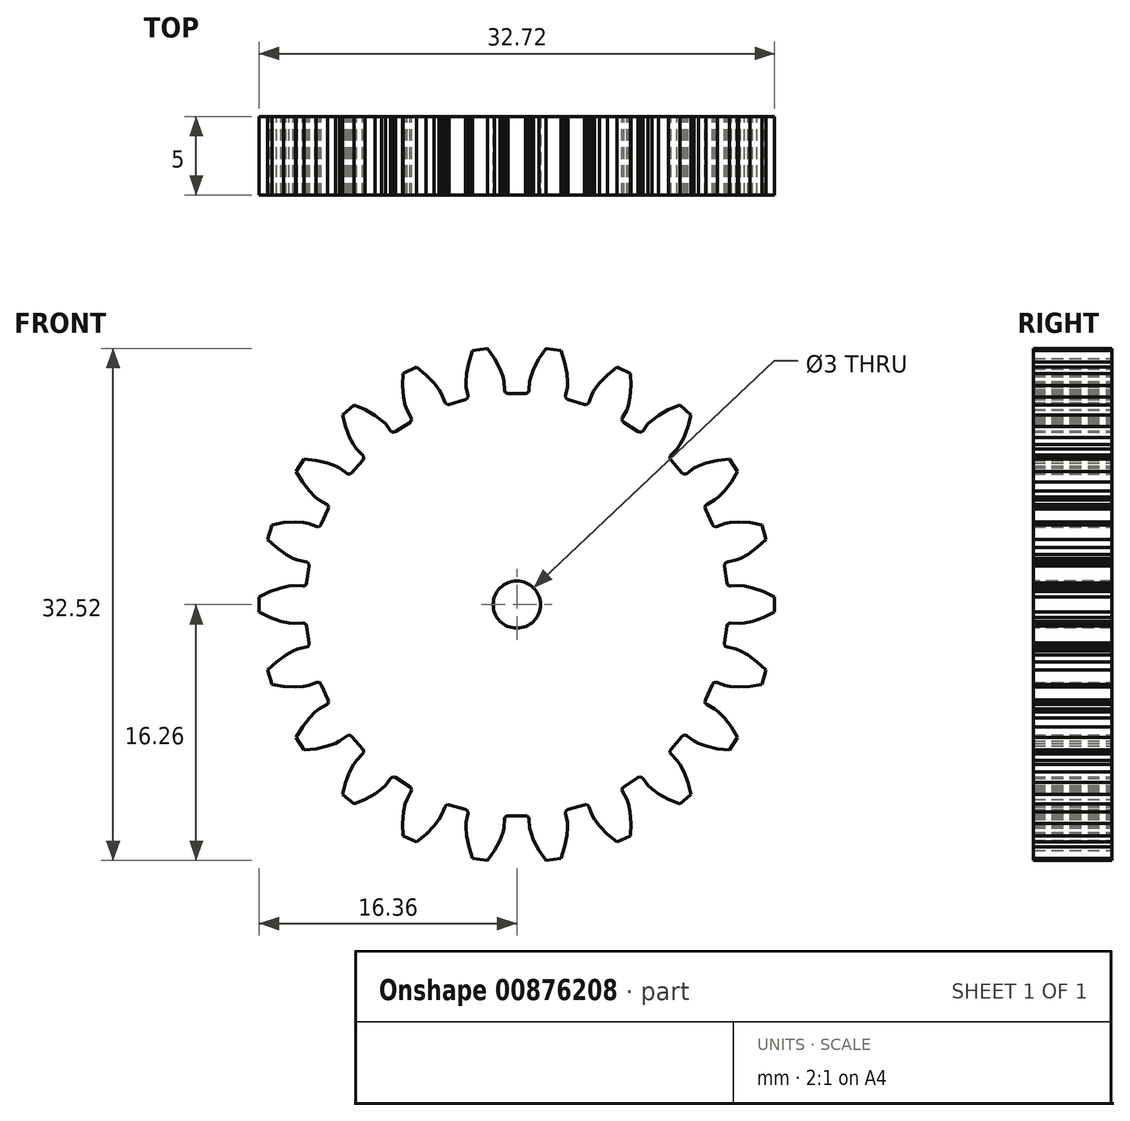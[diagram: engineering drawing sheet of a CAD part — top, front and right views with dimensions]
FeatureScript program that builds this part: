
annotation { "Feature Type Name" : "Feature", "Feature Type Description" : "" }
export const myFeature = defineFeature(function(context is Context, id is Id, definition is map)
    precondition{}
    {
        {
            var Q0;
            Q0=qCreatedBy(makeId("Front.planeOp"),FACE);
            var sketch = newSketch(context, id + "F0", { "sketchPlane" : qUnion([Q0])});
            skLineSegment(sketch, "E0", {"start": v(3.19, -14.67) * mm, "end": v(3.23, -14.15) * mm});
            skLineSegment(sketch, "E1", {"start": v(1.85, 16.26) * mm, "end": v(1.42, 15.62) * mm});
            skLineSegment(sketch, "E2", {"start": v(3.1, 13.28) * mm, "end": v(3.22, 13.83) * mm});
            skLineSegment(sketch, "E3", {"start": v(5.25, 14.06) * mm, "end": v(4.93, 13.65) * mm});
            skLineSegment(sketch, "E4", {"start": v(-9, -12.02) * mm, "end": v(-8.58, -11.7) * mm});
            skLineSegment(sketch, "E5", {"start": v(6.8, -11.58) * mm, "end": v(7.7, -10.99) * mm});
            skLineSegment(sketch, "E6", {"start": v(14.2, -2.94) * mm, "end": v(13.92, -2.82) * mm});
            skLineSegment(sketch, "E7", {"start": v(-0.54, 13.41) * mm, "end": v(-0.65, 13.44) * mm});
            skLineSegment(sketch, "E8", {"start": v(0.54, 13.41) * mm, "end": v(-0.54, 13.41) * mm});
            skLineSegment(sketch, "E9", {"start": v(-0.81, 14.18) * mm, "end": v(-0.89, 14.48) * mm});
            skLineSegment(sketch, "E10", {"start": v(-0.65, 13.44) * mm, "end": v(-0.74, 13.5) * mm});
            skLineSegment(sketch, "E11", {"start": v(-6.71, 11.66) * mm, "end": v(-6.8, 11.58) * mm});
            skLineSegment(sketch, "E12", {"start": v(0.81, 14.18) * mm, "end": v(0.77, 13.61) * mm});
            skLineSegment(sketch, "E13", {"start": v(-9.73, -9.3) * mm, "end": v(-9.73, -9.4) * mm});
            skLineSegment(sketch, "E14", {"start": v(3.1, 13.17) * mm, "end": v(3.1, 13.28) * mm});
            skLineSegment(sketch, "E15", {"start": v(4.57, 12.85) * mm, "end": v(4.51, 12.75) * mm});
            skLineSegment(sketch, "E16", {"start": v(0.89, 14.48) * mm, "end": v(0.81, 14.18) * mm});
            skLineSegment(sketch, "E17", {"start": v(-7.23, -14.68) * mm, "end": v(-6.36, -15.08) * mm});
            skLineSegment(sketch, "E18", {"start": v(-8.58, -11.7) * mm, "end": v(-8.35, -11.49) * mm});
            skLineSegment(sketch, "E19", {"start": v(-1.42, 15.62) * mm, "end": v(-1.85, 16.26) * mm});
            skLineSegment(sketch, "E20", {"start": v(-5.25, -14.06) * mm, "end": v(-4.93, -13.65) * mm});
            skLineSegment(sketch, "E21", {"start": v(3.04, 15.4) * mm, "end": v(2.8, 16.12) * mm});
            skLineSegment(sketch, "E22", {"start": v(-0.74, 13.5) * mm, "end": v(-0.77, 13.61) * mm});
            skLineSegment(sketch, "E23", {"start": v(14.07, -5.24) * mm, "end": v(14.8, -5.2) * mm});
            skLineSegment(sketch, "E24", {"start": v(-4.51, -12.75) * mm, "end": v(-4.41, -12.7) * mm});
            skLineSegment(sketch, "E25", {"start": v(-12.06, -6.36) * mm, "end": v(-12.56, -6.63) * mm});
            skLineSegment(sketch, "E26", {"start": v(-13.4, 1.27) * mm, "end": v(-13.48, 1.2) * mm});
            skLineSegment(sketch, "E27", {"start": v(-0.77, 13.61) * mm, "end": v(-0.81, 14.18) * mm});
            skLineSegment(sketch, "E28", {"start": v(-1.08, 14.97) * mm, "end": v(-1.42, 15.62) * mm});
            skLineSegment(sketch, "E29", {"start": v(-8, -11.04) * mm, "end": v(-7.92, -10.97) * mm});
            skLineSegment(sketch, "E30", {"start": v(-6.8, -11.58) * mm, "end": v(-6.71, -11.66) * mm});
            skLineSegment(sketch, "E31", {"start": v(-14.67, 3.2) * mm, "end": v(-14.2, 2.94) * mm});
            skLineSegment(sketch, "E32", {"start": v(-3.19, -14.67) * mm, "end": v(-3.04, -15.4) * mm});
            skLineSegment(sketch, "E33", {"start": v(0.54, -13.41) * mm, "end": v(0.65, -13.44) * mm});
            skLineSegment(sketch, "E34", {"start": v(-15.26, 3.63) * mm, "end": v(-14.67, 3.2) * mm});
            skLineSegment(sketch, "E35", {"start": v(-13.23, 5.15) * mm, "end": v(-13.54, 5.2) * mm});
            skLineSegment(sketch, "E36", {"start": v(-4.93, -13.65) * mm, "end": v(-4.77, -13.37) * mm});
            skLineSegment(sketch, "E37", {"start": v(-12.06, 6.36) * mm, "end": v(-11.98, 6.28) * mm});
            skLineSegment(sketch, "E38", {"start": v(-16.36, 0.48) * mm, "end": v(-16.36, -0.48) * mm});
            skLineSegment(sketch, "E39", {"start": v(-15.67, 0.82) * mm, "end": v(-16.36, 0.48) * mm});
            skLineSegment(sketch, "E40", {"start": v(3.19, 14.67) * mm, "end": v(3.04, 15.4) * mm});
            skLineSegment(sketch, "E41", {"start": v(3.23, 14.15) * mm, "end": v(3.19, 14.67) * mm});
            skLineSegment(sketch, "E42", {"start": v(3.22, 13.83) * mm, "end": v(3.23, 14.15) * mm});
            skLineSegment(sketch, "E43", {"start": v(-14.02, -8.44) * mm, "end": v(-13.5, -9.25) * mm});
            skLineSegment(sketch, "E44", {"start": v(-13.62, -7.78) * mm, "end": v(-14.02, -8.44) * mm});
            skLineSegment(sketch, "E45", {"start": v(-3.16, 13.08) * mm, "end": v(-3.26, 13.02) * mm});
            skLineSegment(sketch, "E46", {"start": v(-3.1, 13.17) * mm, "end": v(-3.16, 13.08) * mm});
            skLineSegment(sketch, "E47", {"start": v(-3.1, 13.28) * mm, "end": v(-3.1, 13.17) * mm});
            skLineSegment(sketch, "E48", {"start": v(-3.22, 13.83) * mm, "end": v(-3.1, 13.28) * mm});
            skLineSegment(sketch, "E49", {"start": v(-3.23, 14.15) * mm, "end": v(-3.22, 13.83) * mm});
            skLineSegment(sketch, "E50", {"start": v(-3.19, 14.67) * mm, "end": v(-3.23, 14.15) * mm});
            skLineSegment(sketch, "E51", {"start": v(-3.04, 15.4) * mm, "end": v(-3.19, 14.67) * mm});
            skLineSegment(sketch, "E52", {"start": v(-2.8, 16.12) * mm, "end": v(-3.04, 15.4) * mm});
            skLineSegment(sketch, "E53", {"start": v(-1.85, 16.26) * mm, "end": v(-2.8, 16.12) * mm});
            skLineSegment(sketch, "E54", {"start": v(5.76, 14.6) * mm, "end": v(5.25, 14.06) * mm});
            skLineSegment(sketch, "E55", {"start": v(6.36, 15.08) * mm, "end": v(5.76, 14.6) * mm});
            skLineSegment(sketch, "E56", {"start": v(7.23, 14.68) * mm, "end": v(6.36, 15.08) * mm});
            skLineSegment(sketch, "E57", {"start": v(-7.2, 13.18) * mm, "end": v(-7.08, 12.66) * mm});
            skLineSegment(sketch, "E58", {"start": v(-7.25, 13.91) * mm, "end": v(-7.2, 13.18) * mm});
            skLineSegment(sketch, "E59", {"start": v(-7.23, 14.68) * mm, "end": v(-7.25, 13.91) * mm});
            skLineSegment(sketch, "E60", {"start": v(-6.36, 15.08) * mm, "end": v(-7.23, 14.68) * mm});
            skLineSegment(sketch, "E61", {"start": v(-5.76, 14.6) * mm, "end": v(-6.36, 15.08) * mm});
            skLineSegment(sketch, "E62", {"start": v(-5.25, 14.06) * mm, "end": v(-5.76, 14.6) * mm});
            skLineSegment(sketch, "E63", {"start": v(-4.93, 13.65) * mm, "end": v(-5.25, 14.06) * mm});
            skLineSegment(sketch, "E64", {"start": v(-4.77, 13.37) * mm, "end": v(-4.93, 13.65) * mm});
            skLineSegment(sketch, "E65", {"start": v(-4.57, 12.85) * mm, "end": v(-4.77, 13.37) * mm});
            skLineSegment(sketch, "E66", {"start": v(-4.51, 12.75) * mm, "end": v(-4.57, 12.85) * mm});
            skLineSegment(sketch, "E67", {"start": v(1.42, 15.62) * mm, "end": v(1.08, 14.97) * mm});
            skLineSegment(sketch, "E68", {"start": v(-13.54, 5.2) * mm, "end": v(-14.07, 5.24) * mm});
            skLineSegment(sketch, "E69", {"start": v(-0.89, 14.48) * mm, "end": v(-1.08, 14.97) * mm});
            skLineSegment(sketch, "E70", {"start": v(13.17, -7.2) * mm, "end": v(12.8, -6.82) * mm});
            skLineSegment(sketch, "E71", {"start": v(2.8, 16.12) * mm, "end": v(1.85, 16.26) * mm});
            skLineSegment(sketch, "E72", {"start": v(-2.8, -16.12) * mm, "end": v(-1.85, -16.26) * mm});
            skLineSegment(sketch, "E73", {"start": v(-11.97, -6.07) * mm, "end": v(-11.95, -6.17) * mm});
            skLineSegment(sketch, "E74", {"start": v(-6.71, -11.87) * mm, "end": v(-6.98, -12.36) * mm});
            skLineSegment(sketch, "E75", {"start": v(-14.46, 1.18) * mm, "end": v(-14.97, 1.07) * mm});
            skLineSegment(sketch, "E76", {"start": v(-14.07, 5.24) * mm, "end": v(-14.8, 5.2) * mm});
            skLineSegment(sketch, "E77", {"start": v(-1.85, -16.26) * mm, "end": v(-1.42, -15.62) * mm});
            skLineSegment(sketch, "E78", {"start": v(-6.36, -15.08) * mm, "end": v(-5.76, -14.6) * mm});
            skLineSegment(sketch, "E79", {"start": v(-4.3, -12.72) * mm, "end": v(-4.41, -12.7) * mm});
            skLineSegment(sketch, "E80", {"start": v(-7.7, -10.99) * mm, "end": v(-7.81, -10.95) * mm});
            skLineSegment(sketch, "E81", {"start": v(7.23, 14.68) * mm, "end": v(7.25, 13.91) * mm});
            skLineSegment(sketch, "E82", {"start": v(0.74, -13.5) * mm, "end": v(0.77, -13.61) * mm});
            skLineSegment(sketch, "E83", {"start": v(-15.56, 5.07) * mm, "end": v(-14.8, 5.2) * mm});
            skLineSegment(sketch, "E84", {"start": v(-3.22, -13.83) * mm, "end": v(-3.23, -14.15) * mm});
            skLineSegment(sketch, "E85", {"start": v(-15.56, 5.07) * mm, "end": v(-15.83, 4.15) * mm});
            skLineSegment(sketch, "E86", {"start": v(-12.8, -6.82) * mm, "end": v(-13.17, -7.2) * mm});
            skLineSegment(sketch, "E87", {"start": v(-13.23, 5.15) * mm, "end": v(-12.7, 4.96) * mm});
            skLineSegment(sketch, "E88", {"start": v(-5.25, -14.06) * mm, "end": v(-5.76, -14.6) * mm});
            skLineSegment(sketch, "E89", {"start": v(-15.26, 3.63) * mm, "end": v(-15.83, 4.15) * mm});
            skLineSegment(sketch, "E90", {"start": v(13.5, -9.25) * mm, "end": v(12.74, -9.16) * mm});
            skLineSegment(sketch, "E91", {"start": v(-13.2, -2.56) * mm, "end": v(-13.27, -2.65) * mm});
            skLineSegment(sketch, "E92", {"start": v(-12.8, -6.82) * mm, "end": v(-12.56, -6.63) * mm});
            skLineSegment(sketch, "E93", {"start": v(-13.48, -1.2) * mm, "end": v(-13.59, -1.18) * mm});
            skLineSegment(sketch, "E94", {"start": v(-3.16, -13.08) * mm, "end": v(-3.1, -13.17) * mm});
            skLineSegment(sketch, "E95", {"start": v(-0.89, -14.48) * mm, "end": v(-1.08, -14.97) * mm});
            skLineSegment(sketch, "E96", {"start": v(11.53, -8.81) * mm, "end": v(11.24, -8.67) * mm});
            skLineSegment(sketch, "E97", {"start": v(-12.02, -9) * mm, "end": v(-12.74, -9.16) * mm});
            skLineSegment(sketch, "E98", {"start": v(-7.81, -10.95) * mm, "end": v(-7.92, -10.97) * mm});
            skLineSegment(sketch, "E99", {"start": v(-0.54, -13.41) * mm, "end": v(-0.65, -13.44) * mm});
            skLineSegment(sketch, "E100", {"start": v(9.64, -12.38) * mm, "end": v(9, -12.02) * mm});
            skLineSegment(sketch, "E101", {"start": v(-3.1, -13.28) * mm, "end": v(-3.22, -13.83) * mm});
            skLineSegment(sketch, "E102", {"start": v(-3.04, -15.4) * mm, "end": v(-2.8, -16.12) * mm});
            skLineSegment(sketch, "E103", {"start": v(-1.42, -15.62) * mm, "end": v(-1.08, -14.97) * mm});
            skLineSegment(sketch, "E104", {"start": v(-0.89, -14.48) * mm, "end": v(-0.81, -14.18) * mm});
            skLineSegment(sketch, "E105", {"start": v(-0.81, -14.18) * mm, "end": v(-0.77, -13.61) * mm});
            skLineSegment(sketch, "E106", {"start": v(-0.77, -13.61) * mm, "end": v(-0.74, -13.5) * mm});
            skLineSegment(sketch, "E107", {"start": v(-0.74, -13.5) * mm, "end": v(-0.65, -13.44) * mm});
            skLineSegment(sketch, "E108", {"start": v(-0.54, -13.41) * mm, "end": v(0.54, -13.41) * mm});
            skLineSegment(sketch, "E109", {"start": v(0.65, -13.44) * mm, "end": v(0.74, -13.5) * mm});
            skLineSegment(sketch, "E110", {"start": v(0.77, -13.61) * mm, "end": v(0.81, -14.18) * mm});
            skLineSegment(sketch, "E111", {"start": v(0.81, -14.18) * mm, "end": v(0.89, -14.48) * mm});
            skLineSegment(sketch, "E112", {"start": v(0.89, -14.48) * mm, "end": v(1.08, -14.97) * mm});
            skLineSegment(sketch, "E113", {"start": v(1.08, -14.97) * mm, "end": v(1.42, -15.62) * mm});
            skLineSegment(sketch, "E114", {"start": v(1.42, -15.62) * mm, "end": v(1.85, -16.26) * mm});
            skLineSegment(sketch, "E115", {"start": v(-15.26, -3.63) * mm, "end": v(-15.83, -4.15) * mm});
            skLineSegment(sketch, "E116", {"start": v(-15.83, -4.15) * mm, "end": v(-15.56, -5.07) * mm});
            skLineSegment(sketch, "E117", {"start": v(-15.56, -5.07) * mm, "end": v(-14.8, -5.2) * mm});
            skLineSegment(sketch, "E118", {"start": v(-14.67, -3.2) * mm, "end": v(-15.26, -3.63) * mm});
            skLineSegment(sketch, "E119", {"start": v(-14.8, -5.2) * mm, "end": v(-14.07, -5.24) * mm});
            skLineSegment(sketch, "E120", {"start": v(-14.2, -2.94) * mm, "end": v(-14.67, -3.2) * mm});
            skLineSegment(sketch, "E121", {"start": v(-13.92, -2.82) * mm, "end": v(-14.2, -2.94) * mm});
            skLineSegment(sketch, "E122", {"start": v(-14.07, -5.24) * mm, "end": v(-13.54, -5.2) * mm});
            skLineSegment(sketch, "E123", {"start": v(-13.37, -2.7) * mm, "end": v(-13.92, -2.82) * mm});
            skLineSegment(sketch, "E124", {"start": v(-13.54, -5.2) * mm, "end": v(-13.23, -5.15) * mm});
            skLineSegment(sketch, "E125", {"start": v(-13.27, -2.65) * mm, "end": v(-13.37, -2.7) * mm});
            skLineSegment(sketch, "E126", {"start": v(-13.23, -5.15) * mm, "end": v(-12.7, -4.96) * mm});
            skLineSegment(sketch, "E127", {"start": v(-13.2, -2.45) * mm, "end": v(-13.2, -2.56) * mm});
            skLineSegment(sketch, "E128", {"start": v(-13.17, -7.2) * mm, "end": v(-13.62, -7.78) * mm});
            skLineSegment(sketch, "E129", {"start": v(-13.5, -9.25) * mm, "end": v(-12.74, -9.16) * mm});
            skLineSegment(sketch, "E130", {"start": v(-11.98, -6.28) * mm, "end": v(-12.06, -6.36) * mm});
            skLineSegment(sketch, "E131", {"start": v(-12.02, -9) * mm, "end": v(-11.53, -8.81) * mm});
            skLineSegment(sketch, "E132", {"start": v(-11.95, -6.17) * mm, "end": v(-11.98, -6.28) * mm});
            skLineSegment(sketch, "E133", {"start": v(-10.88, -11.3) * mm, "end": v(-11.08, -12.05) * mm});
            skLineSegment(sketch, "E134", {"start": v(-11.08, -12.05) * mm, "end": v(-10.35, -12.68) * mm});
            skLineSegment(sketch, "E135", {"start": v(-10.61, -10.62) * mm, "end": v(-10.88, -11.3) * mm});
            skLineSegment(sketch, "E136", {"start": v(-10.36, -10.15) * mm, "end": v(-10.61, -10.62) * mm});
            skLineSegment(sketch, "E137", {"start": v(-10.18, -9.9) * mm, "end": v(-10.36, -10.15) * mm});
            skLineSegment(sketch, "E138", {"start": v(-10.35, -12.68) * mm, "end": v(-9.64, -12.38) * mm});
            skLineSegment(sketch, "E139", {"start": v(-9.79, -9.5) * mm, "end": v(-10.18, -9.9) * mm});
            skLineSegment(sketch, "E140", {"start": v(-9.73, -9.4) * mm, "end": v(-9.79, -9.5) * mm});
            skLineSegment(sketch, "E141", {"start": v(-7.2, -13.18) * mm, "end": v(-7.25, -13.91) * mm});
            skLineSegment(sketch, "E142", {"start": v(-7.25, -13.91) * mm, "end": v(-7.23, -14.68) * mm});
            skLineSegment(sketch, "E143", {"start": v(-7.08, -12.66) * mm, "end": v(-7.2, -13.18) * mm});
            skLineSegment(sketch, "E144", {"start": v(-6.98, -12.36) * mm, "end": v(-7.08, -12.66) * mm});
            skLineSegment(sketch, "E145", {"start": v(-6.69, -11.76) * mm, "end": v(-6.71, -11.87) * mm});
            skLineSegment(sketch, "E146", {"start": v(-3.23, -14.15) * mm, "end": v(-3.19, -14.67) * mm});
            skLineSegment(sketch, "E147", {"start": v(-7.08, 12.66) * mm, "end": v(-6.98, 12.36) * mm});
            skLineSegment(sketch, "E148", {"start": v(-6.98, 12.36) * mm, "end": v(-6.71, 11.87) * mm});
            skLineSegment(sketch, "E149", {"start": v(-6.71, 11.87) * mm, "end": v(-6.69, 11.76) * mm});
            skLineSegment(sketch, "E150", {"start": v(-4.77, -13.37) * mm, "end": v(-4.57, -12.85) * mm});
            skLineSegment(sketch, "E151", {"start": v(-4.57, -12.85) * mm, "end": v(-4.51, -12.75) * mm});
            skLineSegment(sketch, "E152", {"start": v(-4.41, 12.7) * mm, "end": v(-4.51, 12.75) * mm});
            skLineSegment(sketch, "E153", {"start": v(-4.3, 12.72) * mm, "end": v(-4.41, 12.7) * mm});
            skLineSegment(sketch, "E154", {"start": v(-4.3, -12.72) * mm, "end": v(-3.26, -13.02) * mm});
            skLineSegment(sketch, "E155", {"start": v(-3.26, 13.02) * mm, "end": v(-4.3, 12.72) * mm});
            skLineSegment(sketch, "E156", {"start": v(-3.26, -13.02) * mm, "end": v(-3.16, -13.08) * mm});
            skLineSegment(sketch, "E157", {"start": v(-3.1, -13.17) * mm, "end": v(-3.1, -13.28) * mm});
            skLineSegment(sketch, "E158", {"start": v(-10.35, 12.68) * mm, "end": v(-11.08, 12.05) * mm});
            skLineSegment(sketch, "E159", {"start": v(-11.08, 12.05) * mm, "end": v(-10.88, 11.3) * mm});
            skLineSegment(sketch, "E160", {"start": v(-10.88, 11.3) * mm, "end": v(-10.61, 10.62) * mm});
            skLineSegment(sketch, "E161", {"start": v(-10.61, 10.62) * mm, "end": v(-10.36, 10.15) * mm});
            skLineSegment(sketch, "E162", {"start": v(-10.36, 10.15) * mm, "end": v(-10.18, 9.9) * mm});
            skLineSegment(sketch, "E163", {"start": v(-9.64, 12.38) * mm, "end": v(-10.35, 12.68) * mm});
            skLineSegment(sketch, "E164", {"start": v(-10.18, 9.9) * mm, "end": v(-9.79, 9.5) * mm});
            skLineSegment(sketch, "E165", {"start": v(-9.79, 9.5) * mm, "end": v(-9.73, 9.4) * mm});
            skLineSegment(sketch, "E166", {"start": v(-9.73, 9.4) * mm, "end": v(-9.73, 9.3) * mm});
            skLineSegment(sketch, "E167", {"start": v(-9.64, -12.38) * mm, "end": v(-9, -12.02) * mm});
            skLineSegment(sketch, "E168", {"start": v(-9, 12.02) * mm, "end": v(-9.64, 12.38) * mm});
            skLineSegment(sketch, "E169", {"start": v(-8.58, 11.7) * mm, "end": v(-9, 12.02) * mm});
            skLineSegment(sketch, "E170", {"start": v(-8.35, 11.49) * mm, "end": v(-8.58, 11.7) * mm});
            skLineSegment(sketch, "E171", {"start": v(-8.35, -11.49) * mm, "end": v(-8, -11.04) * mm});
            skLineSegment(sketch, "E172", {"start": v(-8, 11.04) * mm, "end": v(-8.35, 11.49) * mm});
            skLineSegment(sketch, "E173", {"start": v(-7.92, 10.97) * mm, "end": v(-8, 11.04) * mm});
            skLineSegment(sketch, "E174", {"start": v(-7.81, 10.95) * mm, "end": v(-7.92, 10.97) * mm});
            skLineSegment(sketch, "E175", {"start": v(-7.7, 10.99) * mm, "end": v(-7.81, 10.95) * mm});
            skLineSegment(sketch, "E176", {"start": v(-7.7, -10.99) * mm, "end": v(-6.8, -11.58) * mm});
            skLineSegment(sketch, "E177", {"start": v(-6.8, 11.58) * mm, "end": v(-7.7, 10.99) * mm});
            skLineSegment(sketch, "E178", {"start": v(-6.71, -11.66) * mm, "end": v(-6.69, -11.76) * mm});
            skLineSegment(sketch, "E179", {"start": v(-6.69, 11.76) * mm, "end": v(-6.71, 11.66) * mm});
            skLineSegment(sketch, "E180", {"start": v(-13.5, 9.25) * mm, "end": v(-14.02, 8.44) * mm});
            skLineSegment(sketch, "E181", {"start": v(-14.02, 8.44) * mm, "end": v(-13.62, 7.78) * mm});
            skLineSegment(sketch, "E182", {"start": v(-13.62, 7.78) * mm, "end": v(-13.17, 7.2) * mm});
            skLineSegment(sketch, "E183", {"start": v(-12.74, 9.16) * mm, "end": v(-13.5, 9.25) * mm});
            skLineSegment(sketch, "E184", {"start": v(-13.17, 7.2) * mm, "end": v(-12.8, 6.82) * mm});
            skLineSegment(sketch, "E185", {"start": v(-12.8, 6.82) * mm, "end": v(-12.56, 6.63) * mm});
            skLineSegment(sketch, "E186", {"start": v(-12.02, 9) * mm, "end": v(-12.74, 9.16) * mm});
            skLineSegment(sketch, "E187", {"start": v(-12.56, 6.63) * mm, "end": v(-12.06, 6.36) * mm});
            skLineSegment(sketch, "E188", {"start": v(-11.53, 8.81) * mm, "end": v(-12.02, 9) * mm});
            skLineSegment(sketch, "E189", {"start": v(-11.98, 6.28) * mm, "end": v(-11.95, 6.17) * mm});
            skLineSegment(sketch, "E190", {"start": v(-11.53, -8.81) * mm, "end": v(-11.24, -8.67) * mm});
            skLineSegment(sketch, "E191", {"start": v(-11.24, 8.67) * mm, "end": v(-11.53, 8.81) * mm});
            skLineSegment(sketch, "E192", {"start": v(-11.24, -8.67) * mm, "end": v(-10.8, -8.33) * mm});
            skLineSegment(sketch, "E193", {"start": v(-10.8, 8.33) * mm, "end": v(-11.24, 8.67) * mm});
            skLineSegment(sketch, "E194", {"start": v(-10.8, -8.33) * mm, "end": v(-10.7, -8.3) * mm});
            skLineSegment(sketch, "E195", {"start": v(-10.7, 8.3) * mm, "end": v(-10.8, 8.33) * mm});
            skLineSegment(sketch, "E196", {"start": v(-10.7, -8.3) * mm, "end": v(-10.58, -8.3) * mm});
            skLineSegment(sketch, "E197", {"start": v(-10.58, 8.3) * mm, "end": v(-10.7, 8.3) * mm});
            skLineSegment(sketch, "E198", {"start": v(-10.58, -8.3) * mm, "end": v(-10.5, -8.37) * mm});
            skLineSegment(sketch, "E199", {"start": v(-10.5, 8.37) * mm, "end": v(-10.58, 8.3) * mm});
            skLineSegment(sketch, "E200", {"start": v(-10.5, -8.37) * mm, "end": v(-9.78, -9.2) * mm});
            skLineSegment(sketch, "E201", {"start": v(-9.78, 9.2) * mm, "end": v(-10.5, 8.37) * mm});
            skLineSegment(sketch, "E202", {"start": v(-9.78, -9.2) * mm, "end": v(-9.73, -9.3) * mm});
            skLineSegment(sketch, "E203", {"start": v(-9.73, 9.3) * mm, "end": v(-9.78, 9.2) * mm});
            skLineSegment(sketch, "E204", {"start": v(-14.2, 2.94) * mm, "end": v(-13.92, 2.82) * mm});
            skLineSegment(sketch, "E205", {"start": v(-13.92, 2.82) * mm, "end": v(-13.37, 2.7) * mm});
            skLineSegment(sketch, "E206", {"start": v(-13.37, 2.7) * mm, "end": v(-13.27, 2.65) * mm});
            skLineSegment(sketch, "E207", {"start": v(-13.27, 2.65) * mm, "end": v(-13.2, 2.56) * mm});
            skLineSegment(sketch, "E208", {"start": v(-13.2, 2.56) * mm, "end": v(-13.2, 2.45) * mm});
            skLineSegment(sketch, "E209", {"start": v(-12.7, -4.96) * mm, "end": v(-12.6, -4.94) * mm});
            skLineSegment(sketch, "E210", {"start": v(-12.6, 4.94) * mm, "end": v(-12.7, 4.96) * mm});
            skLineSegment(sketch, "E211", {"start": v(-12.6, -4.94) * mm, "end": v(-12.5, -4.99) * mm});
            skLineSegment(sketch, "E212", {"start": v(-12.5, 4.99) * mm, "end": v(-12.6, 4.94) * mm});
            skLineSegment(sketch, "E213", {"start": v(-12.5, -4.99) * mm, "end": v(-12.43, -5.08) * mm});
            skLineSegment(sketch, "E214", {"start": v(-12.43, 5.08) * mm, "end": v(-12.5, 4.99) * mm});
            skLineSegment(sketch, "E215", {"start": v(-12.43, -5.08) * mm, "end": v(-11.97, -6.07) * mm});
            skLineSegment(sketch, "E216", {"start": v(-11.97, 6.07) * mm, "end": v(-12.43, 5.08) * mm});
            skLineSegment(sketch, "E217", {"start": v(-11.95, 6.17) * mm, "end": v(-11.97, 6.07) * mm});
            skLineSegment(sketch, "E218", {"start": v(-16.36, -0.48) * mm, "end": v(-15.67, -0.82) * mm});
            skLineSegment(sketch, "E219", {"start": v(-15.67, -0.82) * mm, "end": v(-14.97, -1.07) * mm});
            skLineSegment(sketch, "E220", {"start": v(-14.97, 1.07) * mm, "end": v(-15.67, 0.82) * mm});
            skLineSegment(sketch, "E221", {"start": v(-14.97, -1.07) * mm, "end": v(-14.46, -1.18) * mm});
            skLineSegment(sketch, "E222", {"start": v(-14.46, -1.18) * mm, "end": v(-14.15, -1.22) * mm});
            skLineSegment(sketch, "E223", {"start": v(-14.15, 1.22) * mm, "end": v(-14.46, 1.18) * mm});
            skLineSegment(sketch, "E224", {"start": v(-14.15, -1.22) * mm, "end": v(-13.59, -1.18) * mm});
            skLineSegment(sketch, "E225", {"start": v(-13.59, 1.18) * mm, "end": v(-14.15, 1.22) * mm});
            skLineSegment(sketch, "E226", {"start": v(-13.48, 1.2) * mm, "end": v(-13.59, 1.18) * mm});
            skLineSegment(sketch, "E227", {"start": v(-13.48, -1.2) * mm, "end": v(-13.4, -1.27) * mm});
            skLineSegment(sketch, "E228", {"start": v(-13.4, -1.27) * mm, "end": v(-13.35, -1.37) * mm});
            skLineSegment(sketch, "E229", {"start": v(-13.35, 1.37) * mm, "end": v(-13.4, 1.27) * mm});
            skLineSegment(sketch, "E230", {"start": v(-13.35, -1.37) * mm, "end": v(-13.2, -2.45) * mm});
            skLineSegment(sketch, "E231", {"start": v(-13.2, 2.45) * mm, "end": v(-13.35, 1.37) * mm});
            skLineSegment(sketch, "E232", {"start": v(0.65, 13.44) * mm, "end": v(0.54, 13.41) * mm});
            skLineSegment(sketch, "E233", {"start": v(0.74, 13.5) * mm, "end": v(0.65, 13.44) * mm});
            skLineSegment(sketch, "E234", {"start": v(0.77, 13.61) * mm, "end": v(0.74, 13.5) * mm});
            skLineSegment(sketch, "E235", {"start": v(1.08, 14.97) * mm, "end": v(0.89, 14.48) * mm});
            skLineSegment(sketch, "E236", {"start": v(1.85, -16.26) * mm, "end": v(2.8, -16.12) * mm});
            skLineSegment(sketch, "E237", {"start": v(2.8, -16.12) * mm, "end": v(3.04, -15.4) * mm});
            skLineSegment(sketch, "E238", {"start": v(3.04, -15.4) * mm, "end": v(3.19, -14.67) * mm});
            skLineSegment(sketch, "E239", {"start": v(3.22, -13.83) * mm, "end": v(3.1, -13.28) * mm});
            skLineSegment(sketch, "E240", {"start": v(3.23, -14.15) * mm, "end": v(3.22, -13.83) * mm});
            skLineSegment(sketch, "E241", {"start": v(3.1, -13.28) * mm, "end": v(3.1, -13.17) * mm});
            skLineSegment(sketch, "E242", {"start": v(3.1, -13.17) * mm, "end": v(3.16, -13.08) * mm});
            skLineSegment(sketch, "E243", {"start": v(3.16, 13.08) * mm, "end": v(3.1, 13.17) * mm});
            skLineSegment(sketch, "E244", {"start": v(3.16, -13.08) * mm, "end": v(3.26, -13.02) * mm});
            skLineSegment(sketch, "E245", {"start": v(3.26, 13.02) * mm, "end": v(3.16, 13.08) * mm});
            skLineSegment(sketch, "E246", {"start": v(3.26, -13.02) * mm, "end": v(4.3, -12.72) * mm});
            skLineSegment(sketch, "E247", {"start": v(4.3, 12.72) * mm, "end": v(3.26, 13.02) * mm});
            skLineSegment(sketch, "E248", {"start": v(4.3, -12.72) * mm, "end": v(4.41, -12.7) * mm});
            skLineSegment(sketch, "E249", {"start": v(4.41, 12.7) * mm, "end": v(4.3, 12.72) * mm});
            skLineSegment(sketch, "E250", {"start": v(4.41, -12.7) * mm, "end": v(4.51, -12.75) * mm});
            skLineSegment(sketch, "E251", {"start": v(4.51, 12.75) * mm, "end": v(4.41, 12.7) * mm});
            skLineSegment(sketch, "E252", {"start": v(4.51, -12.75) * mm, "end": v(4.57, -12.85) * mm});
            skLineSegment(sketch, "E253", {"start": v(4.57, -12.85) * mm, "end": v(4.77, -13.37) * mm});
            skLineSegment(sketch, "E254", {"start": v(4.77, 13.37) * mm, "end": v(4.57, 12.85) * mm});
            skLineSegment(sketch, "E255", {"start": v(4.77, -13.37) * mm, "end": v(4.93, -13.65) * mm});
            skLineSegment(sketch, "E256", {"start": v(4.93, 13.65) * mm, "end": v(4.77, 13.37) * mm});
            skLineSegment(sketch, "E257", {"start": v(4.93, -13.65) * mm, "end": v(5.25, -14.06) * mm});
            skLineSegment(sketch, "E258", {"start": v(5.25, -14.06) * mm, "end": v(5.76, -14.6) * mm});
            skLineSegment(sketch, "E259", {"start": v(5.76, -14.6) * mm, "end": v(6.36, -15.08) * mm});
            skLineSegment(sketch, "E260", {"start": v(6.36, -15.08) * mm, "end": v(7.23, -14.68) * mm});
            skLineSegment(sketch, "E261", {"start": v(6.71, -11.87) * mm, "end": v(6.69, -11.76) * mm});
            skLineSegment(sketch, "E262", {"start": v(6.98, -12.36) * mm, "end": v(6.71, -11.87) * mm});
            skLineSegment(sketch, "E263", {"start": v(7.08, -12.66) * mm, "end": v(6.98, -12.36) * mm});
            skLineSegment(sketch, "E264", {"start": v(7.2, -13.18) * mm, "end": v(7.08, -12.66) * mm});
            skLineSegment(sketch, "E265", {"start": v(7.23, -14.68) * mm, "end": v(7.25, -13.91) * mm});
            skLineSegment(sketch, "E266", {"start": v(7.25, -13.91) * mm, "end": v(7.2, -13.18) * mm});
            skLineSegment(sketch, "E267", {"start": v(6.69, -11.76) * mm, "end": v(6.71, -11.66) * mm});
            skLineSegment(sketch, "E268", {"start": v(6.71, 11.66) * mm, "end": v(6.69, 11.76) * mm});
            skLineSegment(sketch, "E269", {"start": v(6.71, -11.66) * mm, "end": v(6.8, -11.58) * mm});
            skLineSegment(sketch, "E270", {"start": v(6.8, 11.58) * mm, "end": v(6.71, 11.66) * mm});
            skLineSegment(sketch, "E271", {"start": v(7.7, 10.99) * mm, "end": v(6.8, 11.58) * mm});
            skLineSegment(sketch, "E272", {"start": v(7.7, -10.99) * mm, "end": v(7.81, -10.95) * mm});
            skLineSegment(sketch, "E273", {"start": v(7.81, 10.95) * mm, "end": v(7.7, 10.99) * mm});
            skLineSegment(sketch, "E274", {"start": v(7.81, -10.95) * mm, "end": v(7.92, -10.97) * mm});
            skLineSegment(sketch, "E275", {"start": v(7.92, 10.97) * mm, "end": v(7.81, 10.95) * mm});
            skLineSegment(sketch, "E276", {"start": v(7.92, -10.97) * mm, "end": v(8, -11.04) * mm});
            skLineSegment(sketch, "E277", {"start": v(8, 11.04) * mm, "end": v(7.92, 10.97) * mm});
            skLineSegment(sketch, "E278", {"start": v(8, -11.04) * mm, "end": v(8.35, -11.49) * mm});
            skLineSegment(sketch, "E279", {"start": v(8.35, 11.49) * mm, "end": v(8, 11.04) * mm});
            skLineSegment(sketch, "E280", {"start": v(8.35, -11.49) * mm, "end": v(8.58, -11.7) * mm});
            skLineSegment(sketch, "E281", {"start": v(8.58, 11.7) * mm, "end": v(8.35, 11.49) * mm});
            skLineSegment(sketch, "E282", {"start": v(8.58, -11.7) * mm, "end": v(9, -12.02) * mm});
            skLineSegment(sketch, "E283", {"start": v(9, 12.02) * mm, "end": v(8.58, 11.7) * mm});
            skLineSegment(sketch, "E284", {"start": v(9.64, 12.38) * mm, "end": v(9, 12.02) * mm});
            skLineSegment(sketch, "E285", {"start": v(9.73, -9.4) * mm, "end": v(9.73, -9.3) * mm});
            skLineSegment(sketch, "E286", {"start": v(9.64, -12.38) * mm, "end": v(10.35, -12.68) * mm});
            skLineSegment(sketch, "E287", {"start": v(9.79, -9.5) * mm, "end": v(9.73, -9.4) * mm});
            skLineSegment(sketch, "E288", {"start": v(10.18, -9.9) * mm, "end": v(9.79, -9.5) * mm});
            skLineSegment(sketch, "E289", {"start": v(10.36, -10.15) * mm, "end": v(10.18, -9.9) * mm});
            skLineSegment(sketch, "E290", {"start": v(10.35, -12.68) * mm, "end": v(11.08, -12.05) * mm});
            skLineSegment(sketch, "E291", {"start": v(10.61, -10.62) * mm, "end": v(10.36, -10.15) * mm});
            skLineSegment(sketch, "E292", {"start": v(11.08, -12.05) * mm, "end": v(10.88, -11.3) * mm});
            skLineSegment(sketch, "E293", {"start": v(10.88, -11.3) * mm, "end": v(10.61, -10.62) * mm});
            skLineSegment(sketch, "E294", {"start": v(9.73, -9.3) * mm, "end": v(9.78, -9.2) * mm});
            skLineSegment(sketch, "E295", {"start": v(9.78, 9.2) * mm, "end": v(9.73, 9.3) * mm});
            skLineSegment(sketch, "E296", {"start": v(9.78, -9.2) * mm, "end": v(10.5, -8.37) * mm});
            skLineSegment(sketch, "E297", {"start": v(10.5, 8.37) * mm, "end": v(9.78, 9.2) * mm});
            skLineSegment(sketch, "E298", {"start": v(10.5, -8.37) * mm, "end": v(10.58, -8.3) * mm});
            skLineSegment(sketch, "E299", {"start": v(10.58, 8.3) * mm, "end": v(10.5, 8.37) * mm});
            skLineSegment(sketch, "E300", {"start": v(10.58, -8.3) * mm, "end": v(10.7, -8.3) * mm});
            skLineSegment(sketch, "E301", {"start": v(10.7, 8.3) * mm, "end": v(10.58, 8.3) * mm});
            skLineSegment(sketch, "E302", {"start": v(10.7, -8.3) * mm, "end": v(10.8, -8.33) * mm});
            skLineSegment(sketch, "E303", {"start": v(10.8, 8.33) * mm, "end": v(10.7, 8.3) * mm});
            skLineSegment(sketch, "E304", {"start": v(10.8, -8.33) * mm, "end": v(11.24, -8.67) * mm});
            skLineSegment(sketch, "E305", {"start": v(11.24, 8.67) * mm, "end": v(10.8, 8.33) * mm});
            skLineSegment(sketch, "E306", {"start": v(11.53, 8.81) * mm, "end": v(11.24, 8.67) * mm});
            skLineSegment(sketch, "E307", {"start": v(11.53, -8.81) * mm, "end": v(12.02, -9) * mm});
            skLineSegment(sketch, "E308", {"start": v(11.98, -6.28) * mm, "end": v(11.95, -6.17) * mm});
            skLineSegment(sketch, "E309", {"start": v(12.06, -6.36) * mm, "end": v(11.98, -6.28) * mm});
            skLineSegment(sketch, "E310", {"start": v(12.02, -9) * mm, "end": v(12.74, -9.16) * mm});
            skLineSegment(sketch, "E311", {"start": v(12.56, -6.63) * mm, "end": v(12.06, -6.36) * mm});
            skLineSegment(sketch, "E312", {"start": v(12.8, -6.82) * mm, "end": v(12.56, -6.63) * mm});
            skLineSegment(sketch, "E313", {"start": v(13.62, -7.78) * mm, "end": v(13.17, -7.2) * mm});
            skLineSegment(sketch, "E314", {"start": v(13.5, -9.25) * mm, "end": v(14.02, -8.44) * mm});
            skLineSegment(sketch, "E315", {"start": v(14.02, -8.44) * mm, "end": v(13.62, -7.78) * mm});
            skLineSegment(sketch, "E316", {"start": v(11.95, -6.17) * mm, "end": v(11.97, -6.07) * mm});
            skLineSegment(sketch, "E317", {"start": v(11.97, 6.07) * mm, "end": v(11.95, 6.17) * mm});
            skLineSegment(sketch, "E318", {"start": v(11.97, -6.07) * mm, "end": v(12.43, -5.08) * mm});
            skLineSegment(sketch, "E319", {"start": v(12.43, 5.08) * mm, "end": v(11.97, 6.07) * mm});
            skLineSegment(sketch, "E320", {"start": v(12.43, -5.08) * mm, "end": v(12.5, -4.99) * mm});
            skLineSegment(sketch, "E321", {"start": v(12.5, 4.99) * mm, "end": v(12.43, 5.08) * mm});
            skLineSegment(sketch, "E322", {"start": v(12.5, -4.99) * mm, "end": v(12.6, -4.94) * mm});
            skLineSegment(sketch, "E323", {"start": v(12.6, 4.94) * mm, "end": v(12.5, 4.99) * mm});
            skLineSegment(sketch, "E324", {"start": v(12.6, -4.94) * mm, "end": v(12.7, -4.96) * mm});
            skLineSegment(sketch, "E325", {"start": v(12.7, 4.96) * mm, "end": v(12.6, 4.94) * mm});
            skLineSegment(sketch, "E326", {"start": v(12.7, -4.96) * mm, "end": v(13.23, -5.15) * mm});
            skLineSegment(sketch, "E327", {"start": v(13.2, -2.56) * mm, "end": v(13.2, -2.45) * mm});
            skLineSegment(sketch, "E328", {"start": v(13.27, -2.65) * mm, "end": v(13.2, -2.56) * mm});
            skLineSegment(sketch, "E329", {"start": v(13.23, -5.15) * mm, "end": v(13.54, -5.2) * mm});
            skLineSegment(sketch, "E330", {"start": v(13.37, -2.7) * mm, "end": v(13.27, -2.65) * mm});
            skLineSegment(sketch, "E331", {"start": v(13.92, -2.82) * mm, "end": v(13.37, -2.7) * mm});
            skLineSegment(sketch, "E332", {"start": v(13.54, -5.2) * mm, "end": v(14.07, -5.24) * mm});
            skLineSegment(sketch, "E333", {"start": v(14.67, -3.2) * mm, "end": v(14.2, -2.94) * mm});
            skLineSegment(sketch, "E334", {"start": v(15.26, -3.63) * mm, "end": v(14.67, -3.2) * mm});
            skLineSegment(sketch, "E335", {"start": v(14.8, -5.2) * mm, "end": v(15.56, -5.07) * mm});
            skLineSegment(sketch, "E336", {"start": v(15.56, -5.07) * mm, "end": v(15.83, -4.15) * mm});
            skLineSegment(sketch, "E337", {"start": v(15.83, -4.15) * mm, "end": v(15.26, -3.63) * mm});
            skLineSegment(sketch, "E338", {"start": v(13.2, -2.45) * mm, "end": v(13.35, -1.37) * mm});
            skLineSegment(sketch, "E339", {"start": v(13.35, 1.37) * mm, "end": v(13.2, 2.45) * mm});
            skLineSegment(sketch, "E340", {"start": v(13.35, -1.37) * mm, "end": v(13.4, -1.27) * mm});
            skLineSegment(sketch, "E341", {"start": v(13.4, 1.27) * mm, "end": v(13.35, 1.37) * mm});
            skLineSegment(sketch, "E342", {"start": v(13.4, -1.27) * mm, "end": v(13.48, -1.2) * mm});
            skLineSegment(sketch, "E343", {"start": v(13.48, 1.2) * mm, "end": v(13.4, 1.27) * mm});
            skLineSegment(sketch, "E344", {"start": v(13.59, 1.18) * mm, "end": v(13.48, 1.2) * mm});
            skLineSegment(sketch, "E345", {"start": v(13.48, -1.2) * mm, "end": v(13.59, -1.18) * mm});
            skLineSegment(sketch, "E346", {"start": v(13.59, -1.18) * mm, "end": v(14.15, -1.22) * mm});
            skLineSegment(sketch, "E347", {"start": v(14.15, 1.22) * mm, "end": v(13.59, 1.18) * mm});
            skLineSegment(sketch, "E348", {"start": v(14.46, 1.18) * mm, "end": v(14.15, 1.22) * mm});
            skLineSegment(sketch, "E349", {"start": v(14.15, -1.22) * mm, "end": v(14.46, -1.18) * mm});
            skLineSegment(sketch, "E350", {"start": v(14.46, -1.18) * mm, "end": v(14.97, -1.07) * mm});
            skLineSegment(sketch, "E351", {"start": v(14.97, 1.07) * mm, "end": v(14.46, 1.18) * mm});
            skLineSegment(sketch, "E352", {"start": v(14.97, -1.07) * mm, "end": v(15.67, -0.82) * mm});
            skLineSegment(sketch, "E353", {"start": v(15.67, 0.82) * mm, "end": v(14.97, 1.07) * mm});
            skLineSegment(sketch, "E354", {"start": v(15.67, -0.82) * mm, "end": v(16.36, -0.48) * mm});
            skLineSegment(sketch, "E355", {"start": v(16.36, -0.48) * mm, "end": v(16.36, 0.48) * mm});
            skLineSegment(sketch, "E356", {"start": v(16.36, 0.48) * mm, "end": v(15.67, 0.82) * mm});
            skLineSegment(sketch, "E357", {"start": v(13.23, 5.15) * mm, "end": v(12.7, 4.96) * mm});
            skLineSegment(sketch, "E358", {"start": v(13.2, 2.45) * mm, "end": v(13.2, 2.56) * mm});
            skLineSegment(sketch, "E359", {"start": v(13.2, 2.56) * mm, "end": v(13.27, 2.65) * mm});
            skLineSegment(sketch, "E360", {"start": v(13.54, 5.2) * mm, "end": v(13.23, 5.15) * mm});
            skLineSegment(sketch, "E361", {"start": v(13.27, 2.65) * mm, "end": v(13.37, 2.7) * mm});
            skLineSegment(sketch, "E362", {"start": v(13.37, 2.7) * mm, "end": v(13.92, 2.82) * mm});
            skLineSegment(sketch, "E363", {"start": v(14.07, 5.24) * mm, "end": v(13.54, 5.2) * mm});
            skLineSegment(sketch, "E364", {"start": v(13.92, 2.82) * mm, "end": v(14.2, 2.94) * mm});
            skLineSegment(sketch, "E365", {"start": v(14.8, 5.2) * mm, "end": v(14.07, 5.24) * mm});
            skLineSegment(sketch, "E366", {"start": v(14.2, 2.94) * mm, "end": v(14.67, 3.2) * mm});
            skLineSegment(sketch, "E367", {"start": v(14.67, 3.2) * mm, "end": v(15.26, 3.63) * mm});
            skLineSegment(sketch, "E368", {"start": v(15.56, 5.07) * mm, "end": v(14.8, 5.2) * mm});
            skLineSegment(sketch, "E369", {"start": v(15.26, 3.63) * mm, "end": v(15.83, 4.15) * mm});
            skLineSegment(sketch, "E370", {"start": v(15.83, 4.15) * mm, "end": v(15.56, 5.07) * mm});
            skLineSegment(sketch, "E371", {"start": v(12.02, 9) * mm, "end": v(11.53, 8.81) * mm});
            skLineSegment(sketch, "E372", {"start": v(11.95, 6.17) * mm, "end": v(11.98, 6.28) * mm});
            skLineSegment(sketch, "E373", {"start": v(11.98, 6.28) * mm, "end": v(12.06, 6.36) * mm});
            skLineSegment(sketch, "E374", {"start": v(12.74, 9.16) * mm, "end": v(12.02, 9) * mm});
            skLineSegment(sketch, "E375", {"start": v(12.06, 6.36) * mm, "end": v(12.56, 6.63) * mm});
            skLineSegment(sketch, "E376", {"start": v(12.56, 6.63) * mm, "end": v(12.8, 6.82) * mm});
            skLineSegment(sketch, "E377", {"start": v(13.5, 9.25) * mm, "end": v(12.74, 9.16) * mm});
            skLineSegment(sketch, "E378", {"start": v(12.8, 6.82) * mm, "end": v(13.17, 7.2) * mm});
            skLineSegment(sketch, "E379", {"start": v(13.17, 7.2) * mm, "end": v(13.62, 7.78) * mm});
            skLineSegment(sketch, "E380", {"start": v(13.62, 7.78) * mm, "end": v(14.02, 8.44) * mm});
            skLineSegment(sketch, "E381", {"start": v(14.02, 8.44) * mm, "end": v(13.5, 9.25) * mm});
            skLineSegment(sketch, "E382", {"start": v(10.35, 12.68) * mm, "end": v(9.64, 12.38) * mm});
            skLineSegment(sketch, "E383", {"start": v(9.73, 9.3) * mm, "end": v(9.73, 9.4) * mm});
            skLineSegment(sketch, "E384", {"start": v(9.73, 9.4) * mm, "end": v(9.79, 9.5) * mm});
            skLineSegment(sketch, "E385", {"start": v(9.79, 9.5) * mm, "end": v(10.18, 9.9) * mm});
            skLineSegment(sketch, "E386", {"start": v(10.18, 9.9) * mm, "end": v(10.36, 10.15) * mm});
            skLineSegment(sketch, "E387", {"start": v(11.08, 12.05) * mm, "end": v(10.35, 12.68) * mm});
            skLineSegment(sketch, "E388", {"start": v(10.36, 10.15) * mm, "end": v(10.61, 10.62) * mm});
            skLineSegment(sketch, "E389", {"start": v(10.61, 10.62) * mm, "end": v(10.88, 11.3) * mm});
            skLineSegment(sketch, "E390", {"start": v(10.88, 11.3) * mm, "end": v(11.08, 12.05) * mm});
            skLineSegment(sketch, "E391", {"start": v(6.69, 11.76) * mm, "end": v(6.71, 11.87) * mm});
            skLineSegment(sketch, "E392", {"start": v(6.71, 11.87) * mm, "end": v(6.98, 12.36) * mm});
            skLineSegment(sketch, "E393", {"start": v(6.98, 12.36) * mm, "end": v(7.08, 12.66) * mm});
            skLineSegment(sketch, "E394", {"start": v(7.08, 12.66) * mm, "end": v(7.2, 13.18) * mm});
            skLineSegment(sketch, "E395", {"start": v(7.2, 13.18) * mm, "end": v(7.25, 13.91) * mm});
            skSolve(sketch);
        }
        {
            var Q0;
            Q0=qSketchRegion(id+"F0",true);
            extrude(context, id + "F1", {"entities" : qUnion([Q0]), "depth" : 5 * mm, "offsetDistance" : 25 * mm});
        }
        {
            var Q0;
            Q0=makeQuery(id+"F1.opExtrude","CAP_FACE",FACE,{"disambiguationData":[OSD([sQuery(id+"F0.wireOp",EDGE,"E0"),sQuery(id+"F0.wireOp",EDGE,"E1"),sQuery(id+"F0.wireOp",EDGE,"E2"),sQuery(id+"F0.wireOp",EDGE,"E3"),sQuery(id+"F0.wireOp",EDGE,"E4"),sQuery(id+"F0.wireOp",EDGE,"E5"),sQuery(id+"F0.wireOp",EDGE,"E6"),sQuery(id+"F0.wireOp",EDGE,"E7"),sQuery(id+"F0.wireOp",EDGE,"E8"),sQuery(id+"F0.wireOp",EDGE,"E9"),sQuery(id+"F0.wireOp",EDGE,"E10"),sQuery(id+"F0.wireOp",EDGE,"E11"),sQuery(id+"F0.wireOp",EDGE,"E12"),sQuery(id+"F0.wireOp",EDGE,"E13"),sQuery(id+"F0.wireOp",EDGE,"E14"),sQuery(id+"F0.wireOp",EDGE,"E15"),sQuery(id+"F0.wireOp",EDGE,"E16"),sQuery(id+"F0.wireOp",EDGE,"E17"),sQuery(id+"F0.wireOp",EDGE,"E18"),sQuery(id+"F0.wireOp",EDGE,"E19"),sQuery(id+"F0.wireOp",EDGE,"E20"),sQuery(id+"F0.wireOp",EDGE,"E21"),sQuery(id+"F0.wireOp",EDGE,"E22"),sQuery(id+"F0.wireOp",EDGE,"E23"),sQuery(id+"F0.wireOp",EDGE,"E24"),sQuery(id+"F0.wireOp",EDGE,"E25"),sQuery(id+"F0.wireOp",EDGE,"E26"),sQuery(id+"F0.wireOp",EDGE,"E27"),sQuery(id+"F0.wireOp",EDGE,"E28"),sQuery(id+"F0.wireOp",EDGE,"E29"),sQuery(id+"F0.wireOp",EDGE,"E30"),sQuery(id+"F0.wireOp",EDGE,"E31"),sQuery(id+"F0.wireOp",EDGE,"E32"),sQuery(id+"F0.wireOp",EDGE,"E33"),sQuery(id+"F0.wireOp",EDGE,"E34"),sQuery(id+"F0.wireOp",EDGE,"E35"),sQuery(id+"F0.wireOp",EDGE,"E36"),sQuery(id+"F0.wireOp",EDGE,"E37"),sQuery(id+"F0.wireOp",EDGE,"E38"),sQuery(id+"F0.wireOp",EDGE,"E39"),sQuery(id+"F0.wireOp",EDGE,"E40"),sQuery(id+"F0.wireOp",EDGE,"E41"),sQuery(id+"F0.wireOp",EDGE,"E42"),sQuery(id+"F0.wireOp",EDGE,"E43"),sQuery(id+"F0.wireOp",EDGE,"E44"),sQuery(id+"F0.wireOp",EDGE,"E45"),sQuery(id+"F0.wireOp",EDGE,"E46"),sQuery(id+"F0.wireOp",EDGE,"E47"),sQuery(id+"F0.wireOp",EDGE,"E48"),sQuery(id+"F0.wireOp",EDGE,"E49"),sQuery(id+"F0.wireOp",EDGE,"E50"),sQuery(id+"F0.wireOp",EDGE,"E51"),sQuery(id+"F0.wireOp",EDGE,"E52"),sQuery(id+"F0.wireOp",EDGE,"E53"),sQuery(id+"F0.wireOp",EDGE,"E54"),sQuery(id+"F0.wireOp",EDGE,"E55"),sQuery(id+"F0.wireOp",EDGE,"E56"),sQuery(id+"F0.wireOp",EDGE,"E57"),sQuery(id+"F0.wireOp",EDGE,"E58"),sQuery(id+"F0.wireOp",EDGE,"E59"),sQuery(id+"F0.wireOp",EDGE,"E60"),sQuery(id+"F0.wireOp",EDGE,"E61"),sQuery(id+"F0.wireOp",EDGE,"E62"),sQuery(id+"F0.wireOp",EDGE,"E63"),sQuery(id+"F0.wireOp",EDGE,"E64"),sQuery(id+"F0.wireOp",EDGE,"E65"),sQuery(id+"F0.wireOp",EDGE,"E66"),sQuery(id+"F0.wireOp",EDGE,"E67"),sQuery(id+"F0.wireOp",EDGE,"E68"),sQuery(id+"F0.wireOp",EDGE,"E69"),sQuery(id+"F0.wireOp",EDGE,"E70"),sQuery(id+"F0.wireOp",EDGE,"E71"),sQuery(id+"F0.wireOp",EDGE,"E72"),sQuery(id+"F0.wireOp",EDGE,"E73"),sQuery(id+"F0.wireOp",EDGE,"E74"),sQuery(id+"F0.wireOp",EDGE,"E75"),sQuery(id+"F0.wireOp",EDGE,"E76"),sQuery(id+"F0.wireOp",EDGE,"E77"),sQuery(id+"F0.wireOp",EDGE,"E78"),sQuery(id+"F0.wireOp",EDGE,"E79"),sQuery(id+"F0.wireOp",EDGE,"E80"),sQuery(id+"F0.wireOp",EDGE,"E81"),sQuery(id+"F0.wireOp",EDGE,"E82"),sQuery(id+"F0.wireOp",EDGE,"E83"),sQuery(id+"F0.wireOp",EDGE,"E84"),sQuery(id+"F0.wireOp",EDGE,"E85"),sQuery(id+"F0.wireOp",EDGE,"E86"),sQuery(id+"F0.wireOp",EDGE,"E87"),sQuery(id+"F0.wireOp",EDGE,"E88"),sQuery(id+"F0.wireOp",EDGE,"E89"),sQuery(id+"F0.wireOp",EDGE,"E90"),sQuery(id+"F0.wireOp",EDGE,"E91"),sQuery(id+"F0.wireOp",EDGE,"E92"),sQuery(id+"F0.wireOp",EDGE,"E93"),sQuery(id+"F0.wireOp",EDGE,"E94"),sQuery(id+"F0.wireOp",EDGE,"E95"),sQuery(id+"F0.wireOp",EDGE,"E96"),sQuery(id+"F0.wireOp",EDGE,"E97"),sQuery(id+"F0.wireOp",EDGE,"E98"),sQuery(id+"F0.wireOp",EDGE,"E99"),sQuery(id+"F0.wireOp",EDGE,"E100"),sQuery(id+"F0.wireOp",EDGE,"E101"),sQuery(id+"F0.wireOp",EDGE,"E102"),sQuery(id+"F0.wireOp",EDGE,"E103"),sQuery(id+"F0.wireOp",EDGE,"E104"),sQuery(id+"F0.wireOp",EDGE,"E105"),sQuery(id+"F0.wireOp",EDGE,"E106"),sQuery(id+"F0.wireOp",EDGE,"E107"),sQuery(id+"F0.wireOp",EDGE,"E108"),sQuery(id+"F0.wireOp",EDGE,"E109"),sQuery(id+"F0.wireOp",EDGE,"E110"),sQuery(id+"F0.wireOp",EDGE,"E111"),sQuery(id+"F0.wireOp",EDGE,"E112"),sQuery(id+"F0.wireOp",EDGE,"E113"),sQuery(id+"F0.wireOp",EDGE,"E114"),sQuery(id+"F0.wireOp",EDGE,"E115"),sQuery(id+"F0.wireOp",EDGE,"E116"),sQuery(id+"F0.wireOp",EDGE,"E117"),sQuery(id+"F0.wireOp",EDGE,"E118"),sQuery(id+"F0.wireOp",EDGE,"E119"),sQuery(id+"F0.wireOp",EDGE,"E120"),sQuery(id+"F0.wireOp",EDGE,"E121"),sQuery(id+"F0.wireOp",EDGE,"E122"),sQuery(id+"F0.wireOp",EDGE,"E123"),sQuery(id+"F0.wireOp",EDGE,"E124"),sQuery(id+"F0.wireOp",EDGE,"E125"),sQuery(id+"F0.wireOp",EDGE,"E126"),sQuery(id+"F0.wireOp",EDGE,"E127"),sQuery(id+"F0.wireOp",EDGE,"E128"),sQuery(id+"F0.wireOp",EDGE,"E129"),sQuery(id+"F0.wireOp",EDGE,"E130"),sQuery(id+"F0.wireOp",EDGE,"E131"),sQuery(id+"F0.wireOp",EDGE,"E132"),sQuery(id+"F0.wireOp",EDGE,"E133"),sQuery(id+"F0.wireOp",EDGE,"E134"),sQuery(id+"F0.wireOp",EDGE,"E135"),sQuery(id+"F0.wireOp",EDGE,"E136"),sQuery(id+"F0.wireOp",EDGE,"E137"),sQuery(id+"F0.wireOp",EDGE,"E138"),sQuery(id+"F0.wireOp",EDGE,"E139"),sQuery(id+"F0.wireOp",EDGE,"E140"),sQuery(id+"F0.wireOp",EDGE,"E141"),sQuery(id+"F0.wireOp",EDGE,"E142"),sQuery(id+"F0.wireOp",EDGE,"E143"),sQuery(id+"F0.wireOp",EDGE,"E144"),sQuery(id+"F0.wireOp",EDGE,"E145"),sQuery(id+"F0.wireOp",EDGE,"E146"),sQuery(id+"F0.wireOp",EDGE,"E147"),sQuery(id+"F0.wireOp",EDGE,"E148"),sQuery(id+"F0.wireOp",EDGE,"E149"),sQuery(id+"F0.wireOp",EDGE,"E150"),sQuery(id+"F0.wireOp",EDGE,"E151"),sQuery(id+"F0.wireOp",EDGE,"E152"),sQuery(id+"F0.wireOp",EDGE,"E153"),sQuery(id+"F0.wireOp",EDGE,"E154"),sQuery(id+"F0.wireOp",EDGE,"E155"),sQuery(id+"F0.wireOp",EDGE,"E156"),sQuery(id+"F0.wireOp",EDGE,"E157"),sQuery(id+"F0.wireOp",EDGE,"E158"),sQuery(id+"F0.wireOp",EDGE,"E159"),sQuery(id+"F0.wireOp",EDGE,"E160"),sQuery(id+"F0.wireOp",EDGE,"E161"),sQuery(id+"F0.wireOp",EDGE,"E162"),sQuery(id+"F0.wireOp",EDGE,"E163"),sQuery(id+"F0.wireOp",EDGE,"E164"),sQuery(id+"F0.wireOp",EDGE,"E165"),sQuery(id+"F0.wireOp",EDGE,"E166"),sQuery(id+"F0.wireOp",EDGE,"E167"),sQuery(id+"F0.wireOp",EDGE,"E168"),sQuery(id+"F0.wireOp",EDGE,"E169"),sQuery(id+"F0.wireOp",EDGE,"E170"),sQuery(id+"F0.wireOp",EDGE,"E171"),sQuery(id+"F0.wireOp",EDGE,"E172"),sQuery(id+"F0.wireOp",EDGE,"E173"),sQuery(id+"F0.wireOp",EDGE,"E174"),sQuery(id+"F0.wireOp",EDGE,"E175"),sQuery(id+"F0.wireOp",EDGE,"E176"),sQuery(id+"F0.wireOp",EDGE,"E177"),sQuery(id+"F0.wireOp",EDGE,"E178"),sQuery(id+"F0.wireOp",EDGE,"E179"),sQuery(id+"F0.wireOp",EDGE,"E180"),sQuery(id+"F0.wireOp",EDGE,"E181"),sQuery(id+"F0.wireOp",EDGE,"E182"),sQuery(id+"F0.wireOp",EDGE,"E183"),sQuery(id+"F0.wireOp",EDGE,"E184"),sQuery(id+"F0.wireOp",EDGE,"E185"),sQuery(id+"F0.wireOp",EDGE,"E186"),sQuery(id+"F0.wireOp",EDGE,"E187"),sQuery(id+"F0.wireOp",EDGE,"E188"),sQuery(id+"F0.wireOp",EDGE,"E189"),sQuery(id+"F0.wireOp",EDGE,"E190"),sQuery(id+"F0.wireOp",EDGE,"E191"),sQuery(id+"F0.wireOp",EDGE,"E192"),sQuery(id+"F0.wireOp",EDGE,"E193"),sQuery(id+"F0.wireOp",EDGE,"E194"),sQuery(id+"F0.wireOp",EDGE,"E195"),sQuery(id+"F0.wireOp",EDGE,"E196"),sQuery(id+"F0.wireOp",EDGE,"E197"),sQuery(id+"F0.wireOp",EDGE,"E198"),sQuery(id+"F0.wireOp",EDGE,"E199"),sQuery(id+"F0.wireOp",EDGE,"E200"),sQuery(id+"F0.wireOp",EDGE,"E201"),sQuery(id+"F0.wireOp",EDGE,"E202"),sQuery(id+"F0.wireOp",EDGE,"E203"),sQuery(id+"F0.wireOp",EDGE,"E204"),sQuery(id+"F0.wireOp",EDGE,"E205"),sQuery(id+"F0.wireOp",EDGE,"E206"),sQuery(id+"F0.wireOp",EDGE,"E207"),sQuery(id+"F0.wireOp",EDGE,"E208"),sQuery(id+"F0.wireOp",EDGE,"E209"),sQuery(id+"F0.wireOp",EDGE,"E210"),sQuery(id+"F0.wireOp",EDGE,"E211"),sQuery(id+"F0.wireOp",EDGE,"E212"),sQuery(id+"F0.wireOp",EDGE,"E213"),sQuery(id+"F0.wireOp",EDGE,"E214"),sQuery(id+"F0.wireOp",EDGE,"E215"),sQuery(id+"F0.wireOp",EDGE,"E216"),sQuery(id+"F0.wireOp",EDGE,"E217"),sQuery(id+"F0.wireOp",EDGE,"E218"),sQuery(id+"F0.wireOp",EDGE,"E219"),sQuery(id+"F0.wireOp",EDGE,"E220"),sQuery(id+"F0.wireOp",EDGE,"E221"),sQuery(id+"F0.wireOp",EDGE,"E222"),sQuery(id+"F0.wireOp",EDGE,"E223"),sQuery(id+"F0.wireOp",EDGE,"E224"),sQuery(id+"F0.wireOp",EDGE,"E225"),sQuery(id+"F0.wireOp",EDGE,"E226"),sQuery(id+"F0.wireOp",EDGE,"E227"),sQuery(id+"F0.wireOp",EDGE,"E228"),sQuery(id+"F0.wireOp",EDGE,"E229"),sQuery(id+"F0.wireOp",EDGE,"E230"),sQuery(id+"F0.wireOp",EDGE,"E231"),sQuery(id+"F0.wireOp",EDGE,"E232"),sQuery(id+"F0.wireOp",EDGE,"E233"),sQuery(id+"F0.wireOp",EDGE,"E234"),sQuery(id+"F0.wireOp",EDGE,"E235"),sQuery(id+"F0.wireOp",EDGE,"E236"),sQuery(id+"F0.wireOp",EDGE,"E237"),sQuery(id+"F0.wireOp",EDGE,"E238"),sQuery(id+"F0.wireOp",EDGE,"E239"),sQuery(id+"F0.wireOp",EDGE,"E240"),sQuery(id+"F0.wireOp",EDGE,"E241"),sQuery(id+"F0.wireOp",EDGE,"E242"),sQuery(id+"F0.wireOp",EDGE,"E243"),sQuery(id+"F0.wireOp",EDGE,"E244"),sQuery(id+"F0.wireOp",EDGE,"E245"),sQuery(id+"F0.wireOp",EDGE,"E246"),sQuery(id+"F0.wireOp",EDGE,"E247"),sQuery(id+"F0.wireOp",EDGE,"E248"),sQuery(id+"F0.wireOp",EDGE,"E249"),sQuery(id+"F0.wireOp",EDGE,"E250"),sQuery(id+"F0.wireOp",EDGE,"E251"),sQuery(id+"F0.wireOp",EDGE,"E252"),sQuery(id+"F0.wireOp",EDGE,"E253"),sQuery(id+"F0.wireOp",EDGE,"E254"),sQuery(id+"F0.wireOp",EDGE,"E255"),sQuery(id+"F0.wireOp",EDGE,"E256"),sQuery(id+"F0.wireOp",EDGE,"E257"),sQuery(id+"F0.wireOp",EDGE,"E258"),sQuery(id+"F0.wireOp",EDGE,"E259"),sQuery(id+"F0.wireOp",EDGE,"E260"),sQuery(id+"F0.wireOp",EDGE,"E261"),sQuery(id+"F0.wireOp",EDGE,"E262"),sQuery(id+"F0.wireOp",EDGE,"E263"),sQuery(id+"F0.wireOp",EDGE,"E264"),sQuery(id+"F0.wireOp",EDGE,"E265"),sQuery(id+"F0.wireOp",EDGE,"E266"),sQuery(id+"F0.wireOp",EDGE,"E267"),sQuery(id+"F0.wireOp",EDGE,"E268"),sQuery(id+"F0.wireOp",EDGE,"E269"),sQuery(id+"F0.wireOp",EDGE,"E270"),sQuery(id+"F0.wireOp",EDGE,"E271"),sQuery(id+"F0.wireOp",EDGE,"E272"),sQuery(id+"F0.wireOp",EDGE,"E273"),sQuery(id+"F0.wireOp",EDGE,"E274"),sQuery(id+"F0.wireOp",EDGE,"E275"),sQuery(id+"F0.wireOp",EDGE,"E276"),sQuery(id+"F0.wireOp",EDGE,"E277"),sQuery(id+"F0.wireOp",EDGE,"E278"),sQuery(id+"F0.wireOp",EDGE,"E279"),sQuery(id+"F0.wireOp",EDGE,"E280"),sQuery(id+"F0.wireOp",EDGE,"E281"),sQuery(id+"F0.wireOp",EDGE,"E282"),sQuery(id+"F0.wireOp",EDGE,"E283"),sQuery(id+"F0.wireOp",EDGE,"E284"),sQuery(id+"F0.wireOp",EDGE,"E285"),sQuery(id+"F0.wireOp",EDGE,"E286"),sQuery(id+"F0.wireOp",EDGE,"E287"),sQuery(id+"F0.wireOp",EDGE,"E288"),sQuery(id+"F0.wireOp",EDGE,"E289"),sQuery(id+"F0.wireOp",EDGE,"E290"),sQuery(id+"F0.wireOp",EDGE,"E291"),sQuery(id+"F0.wireOp",EDGE,"E292"),sQuery(id+"F0.wireOp",EDGE,"E293"),sQuery(id+"F0.wireOp",EDGE,"E294"),sQuery(id+"F0.wireOp",EDGE,"E295"),sQuery(id+"F0.wireOp",EDGE,"E296"),sQuery(id+"F0.wireOp",EDGE,"E297"),sQuery(id+"F0.wireOp",EDGE,"E298"),sQuery(id+"F0.wireOp",EDGE,"E299"),sQuery(id+"F0.wireOp",EDGE,"E300"),sQuery(id+"F0.wireOp",EDGE,"E301"),sQuery(id+"F0.wireOp",EDGE,"E302"),sQuery(id+"F0.wireOp",EDGE,"E303"),sQuery(id+"F0.wireOp",EDGE,"E304"),sQuery(id+"F0.wireOp",EDGE,"E305"),sQuery(id+"F0.wireOp",EDGE,"E306"),sQuery(id+"F0.wireOp",EDGE,"E307"),sQuery(id+"F0.wireOp",EDGE,"E308"),sQuery(id+"F0.wireOp",EDGE,"E309"),sQuery(id+"F0.wireOp",EDGE,"E310"),sQuery(id+"F0.wireOp",EDGE,"E311"),sQuery(id+"F0.wireOp",EDGE,"E312"),sQuery(id+"F0.wireOp",EDGE,"E313"),sQuery(id+"F0.wireOp",EDGE,"E314"),sQuery(id+"F0.wireOp",EDGE,"E315"),sQuery(id+"F0.wireOp",EDGE,"E316"),sQuery(id+"F0.wireOp",EDGE,"E317"),sQuery(id+"F0.wireOp",EDGE,"E318"),sQuery(id+"F0.wireOp",EDGE,"E319"),sQuery(id+"F0.wireOp",EDGE,"E320"),sQuery(id+"F0.wireOp",EDGE,"E321"),sQuery(id+"F0.wireOp",EDGE,"E322"),sQuery(id+"F0.wireOp",EDGE,"E323"),sQuery(id+"F0.wireOp",EDGE,"E324"),sQuery(id+"F0.wireOp",EDGE,"E325"),sQuery(id+"F0.wireOp",EDGE,"E326"),sQuery(id+"F0.wireOp",EDGE,"E327"),sQuery(id+"F0.wireOp",EDGE,"E328"),sQuery(id+"F0.wireOp",EDGE,"E329"),sQuery(id+"F0.wireOp",EDGE,"E330"),sQuery(id+"F0.wireOp",EDGE,"E331"),sQuery(id+"F0.wireOp",EDGE,"E332"),sQuery(id+"F0.wireOp",EDGE,"E333"),sQuery(id+"F0.wireOp",EDGE,"E334"),sQuery(id+"F0.wireOp",EDGE,"E335"),sQuery(id+"F0.wireOp",EDGE,"E336"),sQuery(id+"F0.wireOp",EDGE,"E337"),sQuery(id+"F0.wireOp",EDGE,"E338"),sQuery(id+"F0.wireOp",EDGE,"E339"),sQuery(id+"F0.wireOp",EDGE,"E340"),sQuery(id+"F0.wireOp",EDGE,"E341"),sQuery(id+"F0.wireOp",EDGE,"E342"),sQuery(id+"F0.wireOp",EDGE,"E343"),sQuery(id+"F0.wireOp",EDGE,"E344"),sQuery(id+"F0.wireOp",EDGE,"E345"),sQuery(id+"F0.wireOp",EDGE,"E346"),sQuery(id+"F0.wireOp",EDGE,"E347"),sQuery(id+"F0.wireOp",EDGE,"E348"),sQuery(id+"F0.wireOp",EDGE,"E349"),sQuery(id+"F0.wireOp",EDGE,"E350"),sQuery(id+"F0.wireOp",EDGE,"E351"),sQuery(id+"F0.wireOp",EDGE,"E352"),sQuery(id+"F0.wireOp",EDGE,"E353"),sQuery(id+"F0.wireOp",EDGE,"E354"),sQuery(id+"F0.wireOp",EDGE,"E355"),sQuery(id+"F0.wireOp",EDGE,"E356"),sQuery(id+"F0.wireOp",EDGE,"E357"),sQuery(id+"F0.wireOp",EDGE,"E358"),sQuery(id+"F0.wireOp",EDGE,"E359"),sQuery(id+"F0.wireOp",EDGE,"E360"),sQuery(id+"F0.wireOp",EDGE,"E361"),sQuery(id+"F0.wireOp",EDGE,"E362"),sQuery(id+"F0.wireOp",EDGE,"E363"),sQuery(id+"F0.wireOp",EDGE,"E364"),sQuery(id+"F0.wireOp",EDGE,"E365"),sQuery(id+"F0.wireOp",EDGE,"E366"),sQuery(id+"F0.wireOp",EDGE,"E367"),sQuery(id+"F0.wireOp",EDGE,"E368"),sQuery(id+"F0.wireOp",EDGE,"E369"),sQuery(id+"F0.wireOp",EDGE,"E370"),sQuery(id+"F0.wireOp",EDGE,"E371"),sQuery(id+"F0.wireOp",EDGE,"E372"),sQuery(id+"F0.wireOp",EDGE,"E373"),sQuery(id+"F0.wireOp",EDGE,"E374"),sQuery(id+"F0.wireOp",EDGE,"E375"),sQuery(id+"F0.wireOp",EDGE,"E376"),sQuery(id+"F0.wireOp",EDGE,"E377"),sQuery(id+"F0.wireOp",EDGE,"E378"),sQuery(id+"F0.wireOp",EDGE,"E379"),sQuery(id+"F0.wireOp",EDGE,"E380"),sQuery(id+"F0.wireOp",EDGE,"E381"),sQuery(id+"F0.wireOp",EDGE,"E382"),sQuery(id+"F0.wireOp",EDGE,"E383"),sQuery(id+"F0.wireOp",EDGE,"E384"),sQuery(id+"F0.wireOp",EDGE,"E385"),sQuery(id+"F0.wireOp",EDGE,"E386"),sQuery(id+"F0.wireOp",EDGE,"E387"),sQuery(id+"F0.wireOp",EDGE,"E388"),sQuery(id+"F0.wireOp",EDGE,"E389"),sQuery(id+"F0.wireOp",EDGE,"E390"),sQuery(id+"F0.wireOp",EDGE,"E391"),sQuery(id+"F0.wireOp",EDGE,"E392"),sQuery(id+"F0.wireOp",EDGE,"E393"),sQuery(id+"F0.wireOp",EDGE,"E394"),sQuery(id+"F0.wireOp",EDGE,"E395")])],"isStart":false});
            var sketch = newSketch(context, id + "F2", { "sketchPlane" : qUnion([Q0])});
            skCircle(sketch, "E396", {"center": v(0, 0) * mm, "radius": 1.5 * mm});
            skSolve(sketch);
        }
        {
            var Q0;
            Q0=qSketchRegion(id+"F2",true);
            extrude(context, id + "F3", {"entities" : qUnion([Q0]), "operationType" : NewBodyOperationType.REMOVE, "endBound" : BoundingType.UP_TO_NEXT, "oppositeDirection" : true, "depth" : 25 * mm, "offsetDistance" : 25 * mm});
        }
    });
